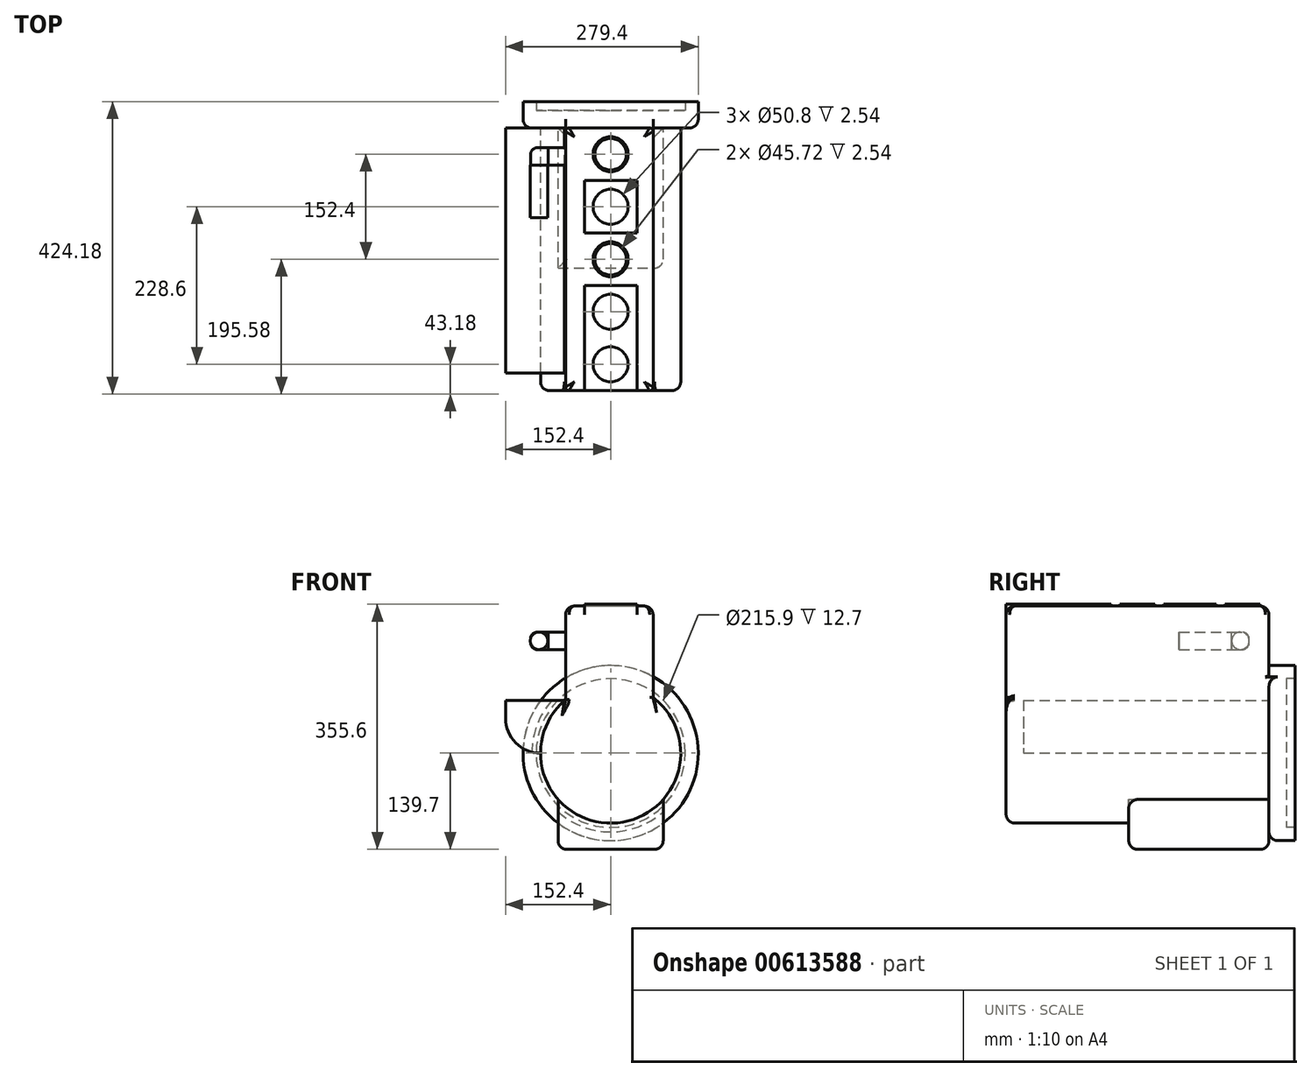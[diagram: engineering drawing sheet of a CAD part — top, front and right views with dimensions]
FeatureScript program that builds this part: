
annotation { "Feature Type Name" : "Feature", "Feature Type Description" : "" }
export const myFeature = defineFeature(function(context is Context, id is Id, definition is map)
    precondition{}
    {
        {
            var Q0;
            Q0=qCreatedBy(makeId("Front.planeOp"),FACE);
            var sketch = newSketch(context, id + "F0", { "sketchPlane" : qUnion([Q0])});
            skLineSegment(sketch, "E0.bottom", {"start": v(38.1, -38.1) * mm, "end": v(-38.1, -38.1) * mm});
            skLineSegment(sketch, "E0.top", {"start": v(38.1, 38.1) * mm, "end": v(-38.1, 38.1) * mm});
            skLineSegment(sketch, "E0.left", {"start": v(38.1, -38.1) * mm, "end": v(38.1, 38.1) * mm});
            skLineSegment(sketch, "E0.right", {"start": v(-38.1, -38.1) * mm, "end": v(-38.1, 38.1) * mm});
            skPoint(sketch, "E0.middle", {"position": v(0, 0) * mm});
            skSolve(sketch);
        }
        {
            var Q0;
            Q0=makeQuery(id+"F0.imprint","IMPRINT",FACE,{"disambiguationData":[TD([[makeQuery(id+"F0.imprint","IMPRINT",EDGE,{"derivedFrom":sQuery(id+"F0.wireOp",EDGE,"E0.bottom")}),-1.0]])]});
            extrude(context, id + "F1", {"entities" : qUnion([Q0]), "depth" : 381 * mm, "offsetDistance" : 25.4 * mm});
        }
        {
            var Q0;
            Q0=makeQuery(id+"F1.opExtrude","SWEPT_FACE",FACE,{"disambiguationData":[OSD([sQuery(id+"F0.wireOp",EDGE,"E0.top")])]});
            var sketch = newSketch(context, id + "F2", { "sketchPlane" : qUnion([Q0])});
            skLineSegment(sketch, "E1", {"start": v(0, 0) * mm, "end": v(0, -381) * mm});
            skCircle(sketch, "E2", {"center": v(0, -342.9) * mm, "radius": 25.4 * mm});
            skLineSegment(sketch, "E3", {"start": v(-38.1, -304.8) * mm, "end": v(38.1, -304.8) * mm});
            skCircle(sketch, "E4.MirrorC", {"center": v(0, -266.7) * mm, "radius": 25.4 * mm});
            skLineSegment(sketch, "E5", {"start": v(-38.1, -228.6) * mm, "end": v(38.1, -228.6) * mm});
            skCircle(sketch, "E6.MirrorC", {"center": v(0, -190.5) * mm, "radius": 25.4 * mm});
            skLineSegment(sketch, "E7", {"start": v(-38.1, -152.4) * mm, "end": v(38.1, -152.4) * mm});
            skCircle(sketch, "E8.MirrorC", {"center": v(0, -114.3) * mm, "radius": 25.4 * mm});
            skLineSegment(sketch, "E9", {"start": v(-38.1, -76.2) * mm, "end": v(38.1, -76.2) * mm});
            skCircle(sketch, "E10.MirrorC", {"center": v(0, -38.1) * mm, "radius": 25.4 * mm});
            skSolve(sketch);
        }
        {
            var Q0;
            {var subQ0=sQuery(id+"F2.wireOp",EDGE,"E8.MirrorC");var subQ1=sQuery(id+"F2.wireOp",EDGE,"E1");var subQ2=makeQuery(id+"F2.imprint","INTERSECT",VERTEX,{"disambiguationData":[OD(0.0)],"derivedFrom":[subQ1,subQ0]});Q0=makeQuery(id+"F2.imprint","IMPRINT",FACE,{"disambiguationData":[TD([[makeQuery(id+"F2.imprint","IMPRINT",EDGE,{"disambiguationData":[TD([[subQ2,-1.0]])],"derivedFrom":subQ1}),-1.0]])]});}
            var Q1;
            {var subQ0=sQuery(id+"F2.wireOp",EDGE,"E8.MirrorC");var subQ1=sQuery(id+"F2.wireOp",EDGE,"E1");var subQ2=makeQuery(id+"F2.imprint","INTERSECT",VERTEX,{"disambiguationData":[OD(0.0)],"derivedFrom":[subQ1,subQ0]});Q1=makeQuery(id+"F2.imprint","IMPRINT",FACE,{"disambiguationData":[TD([[makeQuery(id+"F2.imprint","IMPRINT",EDGE,{"disambiguationData":[TD([[subQ2,-1.0]])],"derivedFrom":subQ1}),1.0]])]});}
            var Q2;
            {var subQ0=sQuery(id+"F2.wireOp",EDGE,"E10.MirrorC");var subQ1=sQuery(id+"F2.wireOp",EDGE,"E1");var subQ2=makeQuery(id+"F2.imprint","INTERSECT",VERTEX,{"disambiguationData":[OD(0.0)],"derivedFrom":[subQ1,subQ0]});Q2=makeQuery(id+"F2.imprint","IMPRINT",FACE,{"disambiguationData":[TD([[makeQuery(id+"F2.imprint","IMPRINT",EDGE,{"disambiguationData":[TD([[subQ2,-1.0]])],"derivedFrom":subQ1}),-1.0]])]});}
            var Q3;
            {var subQ0=sQuery(id+"F2.wireOp",EDGE,"E10.MirrorC");var subQ1=sQuery(id+"F2.wireOp",EDGE,"E1");var subQ2=makeQuery(id+"F2.imprint","INTERSECT",VERTEX,{"disambiguationData":[OD(0.0)],"derivedFrom":[subQ1,subQ0]});Q3=makeQuery(id+"F2.imprint","IMPRINT",FACE,{"disambiguationData":[TD([[makeQuery(id+"F2.imprint","IMPRINT",EDGE,{"disambiguationData":[TD([[subQ2,-1.0]])],"derivedFrom":subQ1}),1.0]])]});}
            var Q4;
            {var subQ0=sQuery(id+"F2.wireOp",EDGE,"E6.MirrorC");var subQ1=sQuery(id+"F2.wireOp",EDGE,"E1");var subQ2=makeQuery(id+"F2.imprint","INTERSECT",VERTEX,{"disambiguationData":[OD(0.0)],"derivedFrom":[subQ1,subQ0]});Q4=makeQuery(id+"F2.imprint","IMPRINT",FACE,{"disambiguationData":[TD([[makeQuery(id+"F2.imprint","IMPRINT",EDGE,{"disambiguationData":[TD([[subQ2,-1.0]])],"derivedFrom":subQ1}),-1.0]])]});}
            var Q5;
            {var subQ0=sQuery(id+"F2.wireOp",EDGE,"E6.MirrorC");var subQ1=sQuery(id+"F2.wireOp",EDGE,"E1");var subQ2=makeQuery(id+"F2.imprint","INTERSECT",VERTEX,{"disambiguationData":[OD(0.0)],"derivedFrom":[subQ1,subQ0]});Q5=makeQuery(id+"F2.imprint","IMPRINT",FACE,{"disambiguationData":[TD([[makeQuery(id+"F2.imprint","IMPRINT",EDGE,{"disambiguationData":[TD([[subQ2,-1.0]])],"derivedFrom":subQ1}),1.0]])]});}
            var Q6;
            {var subQ0=sQuery(id+"F2.wireOp",EDGE,"E4.MirrorC");var subQ1=sQuery(id+"F2.wireOp",EDGE,"E1");var subQ2=makeQuery(id+"F2.imprint","INTERSECT",VERTEX,{"disambiguationData":[OD(0.0)],"derivedFrom":[subQ1,subQ0]});Q6=makeQuery(id+"F2.imprint","IMPRINT",FACE,{"disambiguationData":[TD([[makeQuery(id+"F2.imprint","IMPRINT",EDGE,{"disambiguationData":[TD([[subQ2,-1.0]])],"derivedFrom":subQ1}),-1.0]])]});}
            var Q7;
            {var subQ0=sQuery(id+"F2.wireOp",EDGE,"E4.MirrorC");var subQ1=sQuery(id+"F2.wireOp",EDGE,"E1");var subQ2=makeQuery(id+"F2.imprint","INTERSECT",VERTEX,{"disambiguationData":[OD(0.0)],"derivedFrom":[subQ1,subQ0]});Q7=makeQuery(id+"F2.imprint","IMPRINT",FACE,{"disambiguationData":[TD([[makeQuery(id+"F2.imprint","IMPRINT",EDGE,{"disambiguationData":[TD([[subQ2,-1.0]])],"derivedFrom":subQ1}),1.0]])]});}
            var Q8;
            {var subQ0=sQuery(id+"F2.wireOp",EDGE,"E2");var subQ1=sQuery(id+"F2.wireOp",EDGE,"E1");var subQ2=makeQuery(id+"F2.imprint","INTERSECT",VERTEX,{"disambiguationData":[OD(0.0)],"derivedFrom":[subQ1,subQ0]});Q8=makeQuery(id+"F2.imprint","IMPRINT",FACE,{"disambiguationData":[TD([[makeQuery(id+"F2.imprint","IMPRINT",EDGE,{"disambiguationData":[TD([[subQ2,-1.0]])],"derivedFrom":subQ1}),-1.0]])]});}
            var Q9;
            {var subQ0=sQuery(id+"F2.wireOp",EDGE,"E2");var subQ1=sQuery(id+"F2.wireOp",EDGE,"E1");var subQ2=makeQuery(id+"F2.imprint","INTERSECT",VERTEX,{"disambiguationData":[OD(0.0)],"derivedFrom":[subQ1,subQ0]});Q9=makeQuery(id+"F2.imprint","IMPRINT",FACE,{"disambiguationData":[TD([[makeQuery(id+"F2.imprint","IMPRINT",EDGE,{"disambiguationData":[TD([[subQ2,-1.0]])],"derivedFrom":subQ1}),1.0]])]});}
            extrude(context, id + "F3", {"entities" : qUnion([Q0, Q1, Q2, Q3, Q4, Q5, Q6, Q7, Q8, Q9]), "operationType" : NewBodyOperationType.ADD, "depth" : 177.8 * mm, "offsetDistance" : 25.4 * mm});
        }
        {
            var Q0;
            Q0=qCreatedBy(makeId("Front.planeOp"),FACE);
            var sketch = newSketch(context, id + "F4", { "sketchPlane" : qUnion([Q0])});
            skCircle(sketch, "E11", {"center": v(0, 0) * mm, "radius": 101.6 * mm});
            skSolve(sketch);
        }
        {
            var Q0;
            Q0=makeQuery(id+"F4.imprint","IMPRINT",FACE,{"disambiguationData":[TD([[makeQuery(id+"F4.imprint","IMPRINT",EDGE,{"derivedFrom":sQuery(id+"F4.wireOp",EDGE,"E11")}),1.0]])]});
            extrude(context, id + "F5", {"entities" : qUnion([Q0]), "operationType" : NewBodyOperationType.ADD, "depth" : 381 * mm, "offsetDistance" : 25.4 * mm});
        }
        {
            var Q0;
            Q0=qCreatedBy(makeId("Top.planeOp"),FACE);
            var sketch = newSketch(context, id + "F6", { "sketchPlane" : qUnion([Q0])});
            skLineSegment(sketch, "E12.bottom", {"start": v(-65.36, 0) * mm, "end": v(61.64, 0) * mm});
            skLineSegment(sketch, "E12.top", {"start": v(-65.36, -381) * mm, "end": v(61.64, -381) * mm});
            skLineSegment(sketch, "E12.left", {"start": v(-65.36, 0) * mm, "end": v(-65.36, -381) * mm});
            skLineSegment(sketch, "E12.right", {"start": v(61.64, 0) * mm, "end": v(61.64, -381) * mm});
            skSolve(sketch);
        }
        {
            var Q0;
            Q0 = qSketchRegion(id + "F6", true);
            extrude(context, id + "F7", {"entities" : qUnion([Q0]), "operationType" : NewBodyOperationType.ADD, "depth" : 213.36 * mm, "offsetDistance" : 25.4 * mm});
        }
        {
            var Q0;
            Q0=makeQuery(id+"F7.opExtrude","CAP_FACE",FACE,{"disambiguationData":[OSD([sQuery(id+"F6.wireOp",EDGE,"E12.bottom"),sQuery(id+"F6.wireOp",EDGE,"E12.top"),sQuery(id+"F6.wireOp",EDGE,"E12.left"),sQuery(id+"F6.wireOp",EDGE,"E12.right")])],"isStart":false});
            var sketch = newSketch(context, id + "F8", { "sketchPlane" : qUnion([Q0])});
            skCircle(sketch, "E13", {"center": v(0, -38.1) * mm, "radius": 25.4 * mm});
            skCircle(sketch, "E14", {"center": v(0, -114.3) * mm, "radius": 25.4 * mm});
            skCircle(sketch, "E15", {"center": v(0, -190.5) * mm, "radius": 25.4 * mm});
            skCircle(sketch, "E16", {"center": v(0, -266.7) * mm, "radius": 25.4 * mm});
            skCircle(sketch, "E17", {"center": v(0, -342.9) * mm, "radius": 25.4 * mm});
            skSolve(sketch);
        }
        {
            var Q0;
            Q0=sQuery(id+"F8.wireOp",VERTEX,"E15.center");
            var Q1;
            Q1=sQuery(id+"F8.wireOp",VERTEX,"E16.center");
            var Q2;
            Q2=sQuery(id+"F8.wireOp",VERTEX,"E17.center");
            var Q3;
            Q3=sQuery(id+"F8.wireOp",VERTEX,"E14.center");
            var Q4;
            Q4=sQuery(id+"F8.wireOp",VERTEX,"E13.center");
            var Q5;
            Q5=makeQuery(id+"F1.opExtrude","SWEPT_BODY",BODY,{"disambiguationData":[OSD([sQuery(id+"F0.wireOp",EDGE,"E0.bottom"),sQuery(id+"F0.wireOp",EDGE,"E0.top"),sQuery(id+"F0.wireOp",EDGE,"E0.left"),sQuery(id+"F0.wireOp",EDGE,"E0.right")])]});
            hole(context, id + "F9", {"style" : HoleStyle.SIMPLE, "endStyle" : HoleEndStyle.BLIND, "oppositeDirection" : true, "holeDiameter" : 45.72 * mm, "majorDiameter" : 6.35 * mm, "holeDepth" : 101.6 * mm, "isTappedThrough" : true, "tappedDepth" : 12.7 * mm, "tapClearance" : 3, "locations" : qUnion([Q0, Q1, Q2, Q3, Q4]), "scope" : qUnion([Q5])});
        }
        {
            var Q0;
            Q0=makeQuery(id+"F7.boolean.opBoolean","MERGE",FACE,{"derivedFrom":[makeQuery(id+"F5.boolean.opBoolean","MERGE",FACE,{"derivedFrom":[makeQuery(id+"F1.opExtrude","CAP_FACE",FACE,{"disambiguationData":[OSD([sQuery(id+"F0.wireOp",EDGE,"E0.bottom"),sQuery(id+"F0.wireOp",EDGE,"E0.top"),sQuery(id+"F0.wireOp",EDGE,"E0.left"),sQuery(id+"F0.wireOp",EDGE,"E0.right")])],"isStart":true}),makeQuery(id+"F5.opExtrude","CAP_FACE",FACE,{"disambiguationData":[OSD([sQuery(id+"F4.wireOp",EDGE,"E11")])],"isStart":true})]}),makeQuery(id+"F7.opExtrude","SWEPT_FACE",FACE,{"disambiguationData":[OSD([sQuery(id+"F6.wireOp",EDGE,"E12.bottom")])]})]});
            var sketch = newSketch(context, id + "F10", { "sketchPlane" : qUnion([Q0])});
            skCircle(sketch, "E18", {"center": v(0, 0) * mm, "radius": 127 * mm});
            skCircle(sketch, "E19", {"center": v(0, 0) * mm, "radius": 107.95 * mm});
            skSolve(sketch);
        }
        {
            var Q0;
            {var subQ6=makeQuery(id+"F5.opExtrude","CAP_EDGE",EDGE,{"disambiguationData":[OSD([sQuery(id+"F4.wireOp",EDGE,"E11")])],"isStart":true});Q0=makeQuery(id+"F10.imprint","IMPRINT",FACE,{"disambiguationData":[TD([[makeQuery(id+"F10.imprint","IMPRINT",EDGE,{"derivedFrom":subQ6}),1.0]])]});}
            var Q1;
            {var subQ6=makeQuery(id+"F5.opExtrude","CAP_EDGE",EDGE,{"disambiguationData":[OSD([sQuery(id+"F4.wireOp",EDGE,"E11")])],"isStart":true});Q1=makeQuery(id+"F10.imprint","IMPRINT",FACE,{"disambiguationData":[TD([[makeQuery(id+"F10.imprint","IMPRINT",EDGE,{"derivedFrom":subQ6}),-1.0]])]});}
            extrude(context, id + "F11", {"entities" : qUnion([Q0, Q1]), "operationType" : NewBodyOperationType.ADD, "depth" : 25.4 * mm, "offsetDistance" : 25.4 * mm});
        }
        {
            var Q0;
            Q0 = qSketchRegion(id + "F10", true);
            extrude(context, id + "F12", {"entities" : qUnion([Q0]), "operationType" : NewBodyOperationType.ADD, "depth" : 38.1 * mm, "offsetDistance" : 25.4 * mm});
        }
        {
            var Q0;
            Q0=makeQuery(id+"F7.opExtrude","CAP_EDGE",EDGE,{"disambiguationData":[OSD([sQuery(id+"F6.wireOp",EDGE,"E12.bottom")])],"isStart":false});
            var Q1;
            Q1=makeQuery(id+"F7.opExtrude","CAP_EDGE",EDGE,{"disambiguationData":[OSD([sQuery(id+"F6.wireOp",EDGE,"E12.left")])],"isStart":false});
            var Q2;
            Q2=makeQuery(id+"F7.opExtrude","CAP_EDGE",EDGE,{"disambiguationData":[OSD([sQuery(id+"F6.wireOp",EDGE,"E12.top")])],"isStart":false});
            var Q3;
            Q3=makeQuery(id+"F7.opExtrude","CAP_EDGE",EDGE,{"disambiguationData":[OSD([sQuery(id+"F6.wireOp",EDGE,"E12.right")])],"isStart":false});
            var Q4;
            Q4=makeQuery(id+"F5.opExtrude","CAP_EDGE",EDGE,{"disambiguationData":[OSD([sQuery(id+"F4.wireOp",EDGE,"E11")])],"isStart":false});
            var Q5;
            {var subQ0=sQuery(id+"F10.wireOp",EDGE,"E19");var subQ1=sQuery(id+"F10.wireOp",EDGE,"E18");Q5=makeQuery(id+"F12.boolean.opBoolean","SPLIT",EDGE,{"disambiguationData":[topologyDisambiguationEdgeConnected([makeQuery(id+"F11.opExtrude","CAP_FACE",FACE,{"disambiguationData":[OSD([subQ0])],"isStart":true})])],"derivedFrom":makeQuery(id+"F12.opExtrude","CAP_EDGE",EDGE,{"disambiguationData":[OSD([subQ1])],"isStart":true})});}
            fillet(context, id + "F13", {"entities" : qUnion([Q0, Q1, Q2, Q3, Q4, Q5]), "radius" : 12.7 * mm, "tangentPropagation" : true, "allowEdgeOverflow" : false});
        }
        {
            var Q0;
            Q0=makeQuery(id+"F7.boolean.opBoolean","INTERSECT",EDGE,{"derivedFrom":[makeQuery(id+"F5.opExtrude","SWEPT_FACE",FACE,{"disambiguationData":[OSD([sQuery(id+"F4.wireOp",EDGE,"E11")])]}),makeQuery(id+"F7.opExtrude","SWEPT_FACE",FACE,{"disambiguationData":[OSD([sQuery(id+"F6.wireOp",EDGE,"E12.left")])]})]});
            var Q1;
            Q1=makeQuery(id+"F7.boolean.opBoolean","INTERSECT",EDGE,{"derivedFrom":[makeQuery(id+"F5.opExtrude","SWEPT_FACE",FACE,{"disambiguationData":[OSD([sQuery(id+"F4.wireOp",EDGE,"E11")])]}),makeQuery(id+"F7.opExtrude","SWEPT_FACE",FACE,{"disambiguationData":[OSD([sQuery(id+"F6.wireOp",EDGE,"E12.right")])]})]});
            fillet(context, id + "F14", {"entities" : qUnion([Q0, Q1]), "radius" : 5.08 * mm, "tangentPropagation" : true, "allowEdgeOverflow" : false});
        }
        {
            var Q0;
            Q0=makeQuery(id+"F7.opExtrude","SWEPT_EDGE",EDGE,{"disambiguationData":[OSD([sQuery(id+"F6.wireOp",EDGE,"E12.top"),sQuery(id+"F6.wireOp",EDGE,"E12.right")])]});
            var Q1;
            Q1=makeQuery(id+"F7.opExtrude","SWEPT_EDGE",EDGE,{"disambiguationData":[OSD([sQuery(id+"F6.wireOp",EDGE,"E12.top"),sQuery(id+"F6.wireOp",EDGE,"E12.left")])]});
            var Q2;
            {var subQ0=sQuery(id+"F6.wireOp",EDGE,"E12.bottom");var subQ1=sQuery(id+"F6.wireOp",EDGE,"E12.right");Q2=makeQuery(id+"F12.boolean.opBoolean","SPLIT",EDGE,{"derivedFrom":makeQuery(id+"F11.boolean.opBoolean","SPLIT",EDGE,{"disambiguationData":[topologyDisambiguationEdgeConnected([makeQuery(id+"F5.opExtrude","CAP_FACE",FACE,{"disambiguationData":[OSD([sQuery(id+"F4.wireOp",EDGE,"E11")])],"isStart":true})])],"derivedFrom":makeQuery(id+"F7.opExtrude","SWEPT_EDGE",EDGE,{"disambiguationData":[OSD([subQ0,subQ1])]})})});}
            var Q3;
            {var subQ0=sQuery(id+"F6.wireOp",EDGE,"E12.bottom");var subQ1=sQuery(id+"F6.wireOp",EDGE,"E12.left");Q3=makeQuery(id+"F12.boolean.opBoolean","SPLIT",EDGE,{"derivedFrom":makeQuery(id+"F11.boolean.opBoolean","SPLIT",EDGE,{"disambiguationData":[topologyDisambiguationEdgeConnected([makeQuery(id+"F5.opExtrude","CAP_FACE",FACE,{"disambiguationData":[OSD([sQuery(id+"F4.wireOp",EDGE,"E11")])],"isStart":true})])],"derivedFrom":makeQuery(id+"F7.opExtrude","SWEPT_EDGE",EDGE,{"disambiguationData":[OSD([subQ0,subQ1])]})})});}
            fillet(context, id + "F15", {"entities" : qUnion([Q0, Q1, Q2, Q3]), "radius" : 5.08 * mm, "tangentPropagation" : true, "allowEdgeOverflow" : false});
        }
        {
            var Q0;
            Q0=qCreatedBy(makeId("Top.planeOp"),FACE);
            var sketch = newSketch(context, id + "F16", { "sketchPlane" : qUnion([Q0])});
            skLineSegment(sketch, "E20.bottom", {"start": v(0, 0) * mm, "end": v(-152.4, 0) * mm});
            skLineSegment(sketch, "E20.top", {"start": v(0, -355.6) * mm, "end": v(-152.4, -355.6) * mm});
            skLineSegment(sketch, "E20.left", {"start": v(0, 0) * mm, "end": v(0, -355.6) * mm});
            skLineSegment(sketch, "E20.right", {"start": v(-152.4, 0) * mm, "end": v(-152.4, -355.6) * mm});
            skSolve(sketch);
        }
        {
            var Q0;
            Q0=makeQuery(id+"F16.imprint","IMPRINT",FACE,{"disambiguationData":[TD([[makeQuery(id+"F16.imprint","IMPRINT",EDGE,{"derivedFrom":sQuery(id+"F16.wireOp",EDGE,"E20.bottom")}),1.0]])]});
            extrude(context, id + "F17", {"entities" : qUnion([Q0]), "operationType" : NewBodyOperationType.ADD, "depth" : 76.2 * mm, "offsetDistance" : 25.4 * mm});
        }
        {
            var Q0;
            Q0=makeQuery(id+"F17.opExtrude","CAP_EDGE",EDGE,{"disambiguationData":[OSD([sQuery(id+"F16.wireOp",EDGE,"E20.right")])],"isStart":true});
            fillet(context, id + "F18", {"entities" : qUnion([Q0]), "radius" : 50.8 * mm, "tangentPropagation" : true, "allowEdgeOverflow" : false});
        }
        {
            var Q0;
            Q0=qCreatedBy(makeId("Top.planeOp"),FACE);
            var sketch = newSketch(context, id + "F19", { "sketchPlane" : qUnion([Q0])});
            skLineSegment(sketch, "E21.bottom", {"start": v(0, 0) * mm, "end": v(76.2, 0) * mm});
            skLineSegment(sketch, "E21.top", {"start": v(0, -203.2) * mm, "end": v(76.2, -203.2) * mm});
            skLineSegment(sketch, "E21.left", {"start": v(0, 0) * mm, "end": v(0, -203.2) * mm});
            skLineSegment(sketch, "E21.right", {"start": v(76.2, 0) * mm, "end": v(76.2, -203.2) * mm});
            skLineSegment(sketch, "E22.MirrorCS", {"start": v(0, -203.2) * mm, "end": v(-76.2, -203.2) * mm});
            skLineSegment(sketch, "E23.MirrorCS", {"start": v(-76.2, 0) * mm, "end": v(-76.2, -203.2) * mm});
            skLineSegment(sketch, "E24.MirrorCS", {"start": v(0, 0) * mm, "end": v(-76.2, 0) * mm});
            skSolve(sketch);
        }
        {
            var Q0;
            Q0 = qSketchRegion(id + "F19", true);
            extrude(context, id + "F20", {"entities" : qUnion([Q0]), "operationType" : NewBodyOperationType.ADD, "oppositeDirection" : true, "depth" : 139.7 * mm, "offsetDistance" : 25.4 * mm});
        }
        {
            var Q0;
            Q0=makeQuery(id+"F20.opExtrude","CAP_EDGE",EDGE,{"disambiguationData":[OSD([sQuery(id+"F19.wireOp",EDGE,"E21.right")])],"isStart":false});
            var Q1;
            Q1=makeQuery(id+"F20.opExtrude","SWEPT_EDGE",EDGE,{"disambiguationData":[OSD([sQuery(id+"F19.wireOp",EDGE,"E21.top"),sQuery(id+"F19.wireOp",EDGE,"E21.right")])]});
            var Q2;
            Q2=makeQuery(id+"F20.opExtrude","CAP_EDGE",EDGE,{"disambiguationData":[OSD([sQuery(id+"F19.wireOp",EDGE,"E21.bottom"),sQuery(id+"F19.wireOp",EDGE,"E24.MirrorCS")])],"isStart":false});
            var Q3;
            Q3=makeQuery(id+"F20.opExtrude","CAP_EDGE",EDGE,{"disambiguationData":[OSD([sQuery(id+"F19.wireOp",EDGE,"E21.top"),sQuery(id+"F19.wireOp",EDGE,"E22.MirrorCS")])],"isStart":false});
            var Q4;
            Q4=makeQuery(id+"F20.opExtrude","CAP_EDGE",EDGE,{"disambiguationData":[OSD([sQuery(id+"F19.wireOp",EDGE,"E23.MirrorCS")])],"isStart":false});
            fillet(context, id + "F21", {"entities" : qUnion([Q0, Q1, Q2, Q3, Q4]), "radius" : 12.7 * mm, "tangentPropagation" : true, "allowEdgeOverflow" : false});
        }
        {
            var Q0;
            Q0=makeQuery(id+"F7.opExtrude","SWEPT_FACE",FACE,{"disambiguationData":[OSD([sQuery(id+"F6.wireOp",EDGE,"E12.left")])]});
            var sketch = newSketch(context, id + "F22", { "sketchPlane" : qUnion([Q0])});
            skCircle(sketch, "E25", {"center": v(41.36, 162.9) * mm, "radius": 12.7 * mm});
            skSolve(sketch);
        }
        {
            var Q0;
            Q0=makeQuery(id+"F22.imprint","IMPRINT",FACE,{"disambiguationData":[TD([[makeQuery(id+"F22.imprint","IMPRINT",EDGE,{"derivedFrom":sQuery(id+"F22.wireOp",EDGE,"E25")}),1.0]])]});
            extrude(context, id + "F23", {"entities" : qUnion([Q0]), "operationType" : NewBodyOperationType.ADD, "depth" : 25.4 * mm, "offsetDistance" : 25.4 * mm});
        }
        {
            var Q0;
            Q0=makeQuery(id+"F23.opExtrude","CAP_FACE",FACE,{"disambiguationData":[OSD([sQuery(id+"F22.wireOp",EDGE,"E25")])],"isStart":false});
            var sketch = newSketch(context, id + "F24", { "sketchPlane" : qUnion([Q0])});
            skLineSegment(sketch, "E26.bottom", {"start": v(54.06, 150.2) * mm, "end": v(28.66, 150.2) * mm});
            skLineSegment(sketch, "E26.top", {"start": v(54.06, 175.6) * mm, "end": v(28.66, 175.6) * mm});
            skLineSegment(sketch, "E26.left", {"start": v(54.06, 150.2) * mm, "end": v(54.06, 175.6) * mm});
            skLineSegment(sketch, "E26.right", {"start": v(28.66, 150.2) * mm, "end": v(28.66, 175.6) * mm});
            skPoint(sketch, "E26.middle", {"position": v(41.36, 162.9) * mm});
            skSolve(sketch);
        }
        {
            var Q0;
            {var subQ0=sQuery(id+"F24.wireOp",EDGE,"E26.left");var subQ1=sQuery(id+"F24.wireOp",EDGE,"E26.bottom");var subQ2=makeQuery(id+"F24.imprint","INTERSECT",VERTEX,{"derivedFrom":[subQ1,subQ0]});Q0=makeQuery(id+"F24.imprint","IMPRINT",FACE,{"disambiguationData":[TD([[makeQuery(id+"F24.imprint","IMPRINT",EDGE,{"disambiguationData":[TD([[subQ2,-1.0]])],"derivedFrom":subQ1}),-1.0]])]});}
            var Q1;
            {var subQ0=sQuery(id+"F24.wireOp",EDGE,"E26.left");var subQ1=sQuery(id+"F24.wireOp",EDGE,"E26.top");var subQ2=makeQuery(id+"F24.imprint","INTERSECT",VERTEX,{"derivedFrom":[subQ1,subQ0]});Q1=makeQuery(id+"F24.imprint","IMPRINT",FACE,{"disambiguationData":[TD([[makeQuery(id+"F24.imprint","IMPRINT",EDGE,{"disambiguationData":[TD([[subQ2,-1.0]])],"derivedFrom":subQ1}),1.0]])]});}
            var Q2;
            {var subQ0=sQuery(id+"F24.wireOp",EDGE,"E26.right");var subQ1=sQuery(id+"F24.wireOp",EDGE,"E26.top");var subQ2=makeQuery(id+"F24.imprint","INTERSECT",VERTEX,{"derivedFrom":[subQ1,subQ0]});Q2=makeQuery(id+"F24.imprint","IMPRINT",FACE,{"disambiguationData":[TD([[makeQuery(id+"F24.imprint","IMPRINT",EDGE,{"disambiguationData":[TD([[subQ2,1.0]])],"derivedFrom":subQ1}),1.0]])]});}
            var Q3;
            {var subQ0=sQuery(id+"F24.wireOp",EDGE,"E26.right");var subQ1=sQuery(id+"F24.wireOp",EDGE,"E26.bottom");var subQ2=makeQuery(id+"F24.imprint","INTERSECT",VERTEX,{"derivedFrom":[subQ1,subQ0]});Q3=makeQuery(id+"F24.imprint","IMPRINT",FACE,{"disambiguationData":[TD([[makeQuery(id+"F24.imprint","IMPRINT",EDGE,{"disambiguationData":[TD([[subQ2,1.0]])],"derivedFrom":subQ1}),-1.0]])]});}
            var Q4;
            {var subQ0=makeQuery(id+"F23.opExtrude","CAP_EDGE",EDGE,{"disambiguationData":[OSD([sQuery(id+"F22.wireOp",EDGE,"E25")])],"isStart":false});var subQ1=makeQuery(id+"F24.imprint","INTERSECT",VERTEX,{"derivedFrom":[subQ0,sQuery(id+"F24.wireOp",EDGE,"E26.bottom")]});Q4=makeQuery(id+"F24.imprint","IMPRINT",FACE,{"disambiguationData":[TD([[makeQuery(id+"F24.imprint","IMPRINT",EDGE,{"disambiguationData":[TD([[subQ1,-1.0]])],"derivedFrom":subQ0}),1.0]])]});}
            extrude(context, id + "F25", {"entities" : qUnion([Q0, Q1, Q2, Q3, Q4]), "operationType" : NewBodyOperationType.ADD, "depth" : 25.4 * mm, "offsetDistance" : 25.4 * mm});
        }
        {
            var Q0;
            Q0=makeQuery(id+"F25.opExtrude","SWEPT_FACE",FACE,{"disambiguationData":[OSD([sQuery(id+"F24.wireOp",EDGE,"E26.left")])]});
            var sketch = newSketch(context, id + "F26", { "sketchPlane" : qUnion([Q0])});
            skCircle(sketch, "E27", {"center": v(-103.76, 162.9) * mm, "radius": 12.7 * mm});
            skSolve(sketch);
        }
        {
            var Q0;
            Q0 = qSketchRegion(id + "F26", true);
            extrude(context, id + "F27", {"entities" : qUnion([Q0]), "operationType" : NewBodyOperationType.ADD, "depth" : 76.2 * mm, "offsetDistance" : 25.4 * mm});
        }
        {
            var Q0;
            Q0=makeQuery(id+"F25.opExtrude","CAP_EDGE",EDGE,{"disambiguationData":[OSD([sQuery(id+"F24.wireOp",EDGE,"E26.top")])],"isStart":false});
            var Q1;
            Q1=makeQuery(id+"F25.opExtrude","CAP_EDGE",EDGE,{"disambiguationData":[OSD([sQuery(id+"F24.wireOp",EDGE,"E26.bottom")])],"isStart":false});
            var Q2;
            Q2=makeQuery(id+"F25.opExtrude","CAP_EDGE",EDGE,{"disambiguationData":[OSD([sQuery(id+"F24.wireOp",EDGE,"E26.right")])],"isStart":false});
            var Q3;
            Q3=makeQuery(id+"F25.opExtrude","SWEPT_EDGE",EDGE,{"disambiguationData":[OSD([sQuery(id+"F24.wireOp",EDGE,"E26.bottom"),sQuery(id+"F24.wireOp",EDGE,"E26.right")])]});
            var Q4;
            Q4=makeQuery(id+"F25.opExtrude","SWEPT_EDGE",EDGE,{"disambiguationData":[OSD([sQuery(id+"F24.wireOp",EDGE,"E26.top"),sQuery(id+"F24.wireOp",EDGE,"E26.right")])]});
            fillet(context, id + "F28", {"entities" : qUnion([Q0, Q1, Q2, Q3, Q4]), "radius" : 10.16 * mm, "tangentPropagation" : true, "allowEdgeOverflow" : false});
        }
    });
